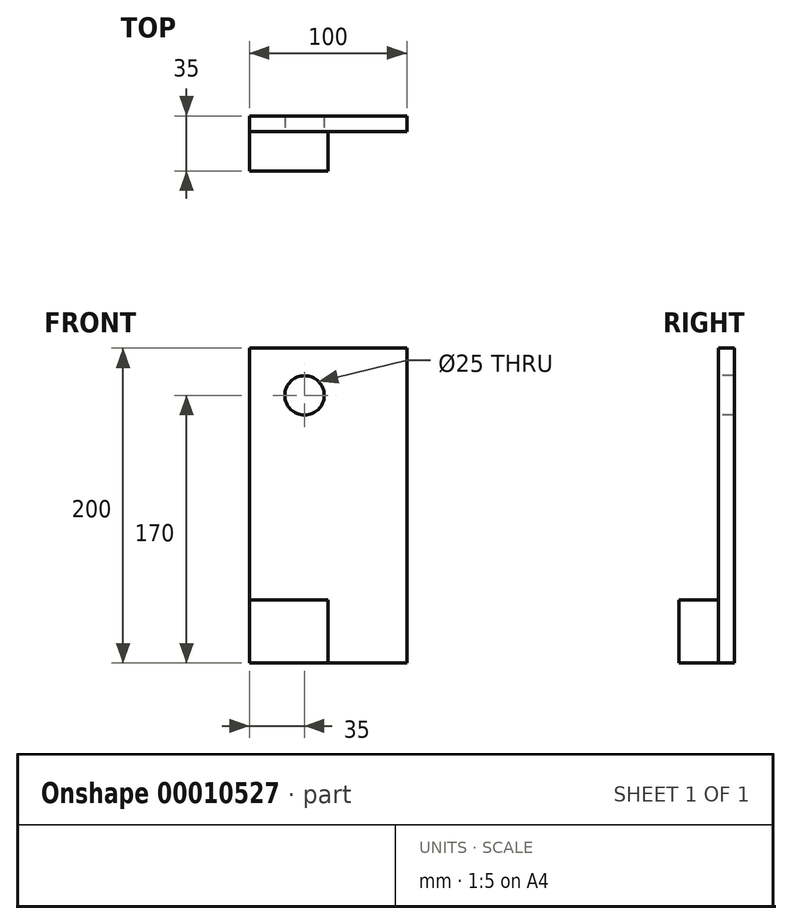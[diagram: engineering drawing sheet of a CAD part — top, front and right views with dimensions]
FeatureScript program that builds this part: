
annotation { "Feature Type Name" : "Feature", "Feature Type Description" : "" }
export const myFeature = defineFeature(function(context is Context, id is Id, definition is map)
    precondition{}
    {
        {
            var Q0;
            Q0=qCreatedBy(makeId("Front.planeOp"),FACE);
            var sketch = newSketch(context, id + "F0", { "sketchPlane" : qUnion([Q0])});
            skLineSegment(sketch, "E0.bottom", {"start": v(0, 0) * mm, "end": v(100, 0) * mm});
            skLineSegment(sketch, "E0.top", {"start": v(0, 200) * mm, "end": v(100, 200) * mm});
            skLineSegment(sketch, "E0.left", {"start": v(0, 0) * mm, "end": v(0, 200) * mm});
            skLineSegment(sketch, "E0.right", {"start": v(100, 0) * mm, "end": v(100, 200) * mm});
            skSolve(sketch);
        }
        {
            var Q0;
            Q0 = qSketchRegion(id + "F0", true);
            extrude(context, id + "F1", {"entities" : qUnion([Q0]), "oppositeDirection" : true, "depth" : 10 * mm});
        }
        {
            var Q0;
            Q0=makeQuery(id+"F1.opExtrude","CAP_FACE",FACE,{"disambiguationData":[OSD([sQuery(id+"F0.wireOp",EDGE,"E0.bottom"),sQuery(id+"F0.wireOp",EDGE,"E0.top"),sQuery(id+"F0.wireOp",EDGE,"E0.left"),sQuery(id+"F0.wireOp",EDGE,"E0.right")])],"isStart":true});
            var sketch = newSketch(context, id + "F2", { "sketchPlane" : qUnion([Q0])});
            skLineSegment(sketch, "E1.bottom", {"start": v(0, 0) * mm, "end": v(50, 0) * mm});
            skLineSegment(sketch, "E1.top", {"start": v(0, 40) * mm, "end": v(50, 40) * mm});
            skLineSegment(sketch, "E1.left", {"start": v(0, 0) * mm, "end": v(0, 40) * mm});
            skLineSegment(sketch, "E1.right", {"start": v(50, 0) * mm, "end": v(50, 40) * mm});
            skSolve(sketch);
        }
        {
            var Q0;
            Q0 = qSketchRegion(id + "F2", true);
            extrude(context, id + "F3", {"entities" : qUnion([Q0]), "operationType" : NewBodyOperationType.ADD, "depth" : 25 * mm});
        }
        {
            var Q0;
            Q0=makeQuery(id+"F1.opExtrude","CAP_FACE",FACE,{"disambiguationData":[OSD([sQuery(id+"F0.wireOp",EDGE,"E0.bottom"),sQuery(id+"F0.wireOp",EDGE,"E0.top"),sQuery(id+"F0.wireOp",EDGE,"E0.left"),sQuery(id+"F0.wireOp",EDGE,"E0.right")])],"isStart":true});
            var sketch = newSketch(context, id + "F4", { "sketchPlane" : qUnion([Q0])});
            skPoint(sketch, "E2", {"position": v(35, 170) * mm});
            skSolve(sketch);
        }
        {
            var Q0;
            Q0=sQuery(id+"F4.wireOp",VERTEX,"E2");
            var Q1;
            Q1=makeQuery(id+"F1.opExtrude","SWEPT_BODY",BODY,{"disambiguationData":[OSD([sQuery(id+"F0.wireOp",EDGE,"E0.bottom"),sQuery(id+"F0.wireOp",EDGE,"E0.top"),sQuery(id+"F0.wireOp",EDGE,"E0.left"),sQuery(id+"F0.wireOp",EDGE,"E0.right")])]});
            hole(context, id + "F5", {"style" : HoleStyle.SIMPLE, "endStyle" : HoleEndStyle.THROUGH, "holeDiameter" : 25 * mm, "isTappedThrough" : true, "tappedDepth" : 12 * mm, "tapClearance" : 3, "locations" : qUnion([Q0]), "scope" : qUnion([Q1])});
        }
    });
